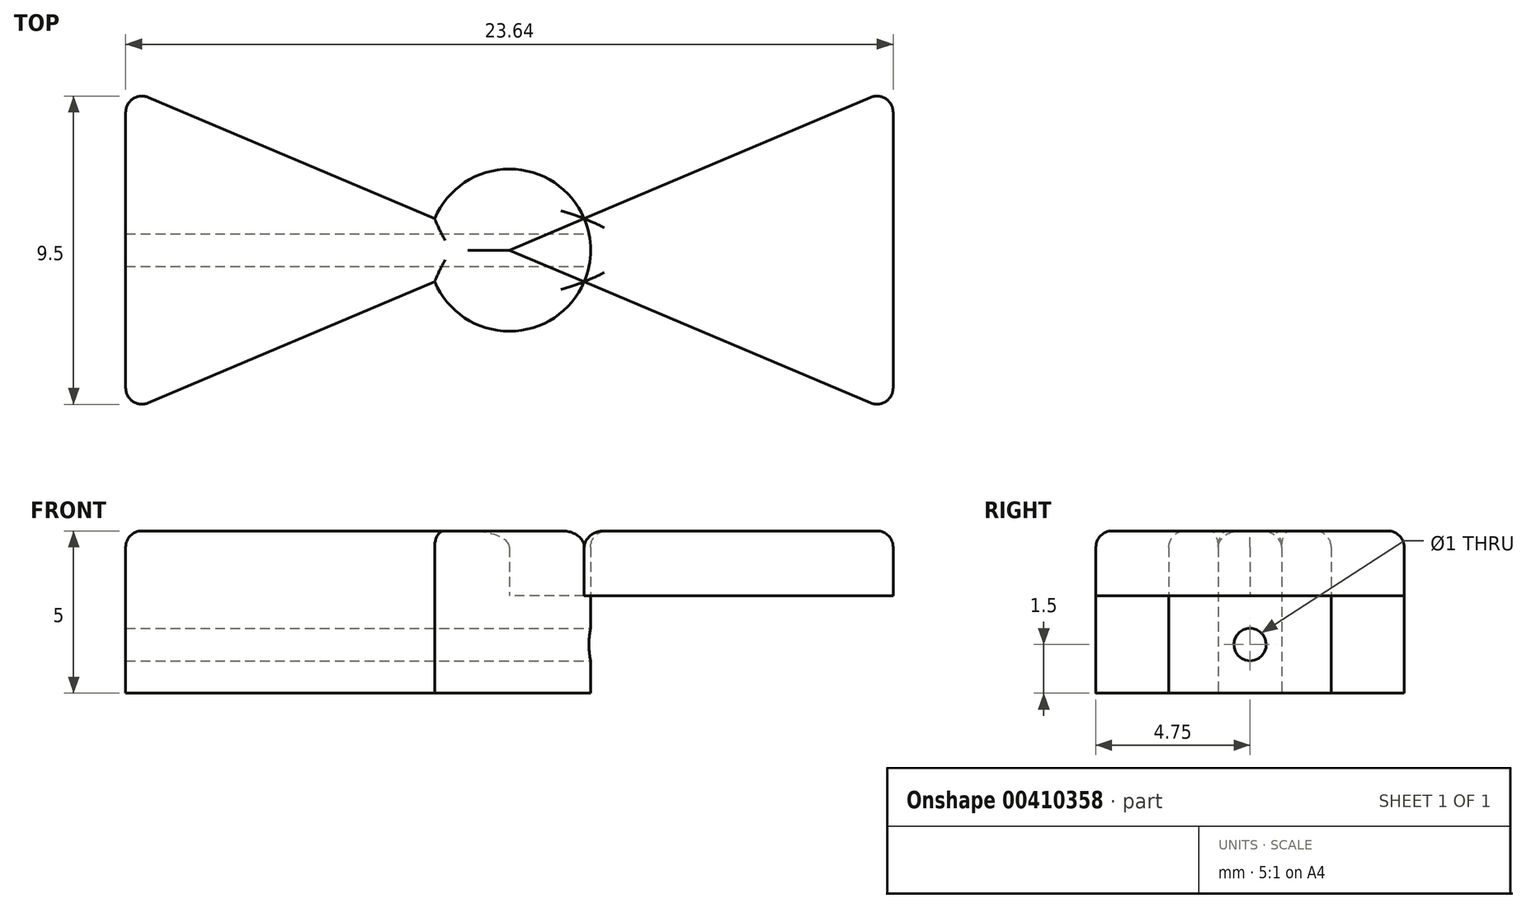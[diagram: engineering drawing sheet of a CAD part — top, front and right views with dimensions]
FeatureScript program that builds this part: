
annotation { "Feature Type Name" : "Feature", "Feature Type Description" : "" }
export const myFeature = defineFeature(function(context is Context, id is Id, definition is map)
    precondition{}
    {
        {
            var Q0;
            Q0=qCreatedBy(makeId("Top.planeOp"),FACE);
            var sketch = newSketch(context, id + "F0", { "sketchPlane" : qUnion([Q0])});
            skCircle(sketch, "E0", {"center": v(0, 0) * mm, "radius": 2.5 * mm});
            skLineSegment(sketch, "E1", {"start": v(-13.8, 0) * mm, "end": v(16.45, 0) * mm, "construction": true});
            skLineSegment(sketch, "E2", {"start": v(0, 11.69) * mm, "end": v(0, -11.19) * mm, "construction": true});
            skLineSegment(sketch, "E3", {"start": v(-11.82, 5) * mm, "end": v(-11.82, -5) * mm});
            skLineSegment(sketch, "E4", {"start": v(-11.82, -5) * mm, "end": v(11.82, 5) * mm});
            skLineSegment(sketch, "E5", {"start": v(11.82, 5) * mm, "end": v(11.82, -5) * mm});
            skLineSegment(sketch, "E6", {"start": v(11.82, -5) * mm, "end": v(-11.82, 5) * mm});
            skLineSegment(sketch, "E7", {"start": v(-11.82, 5) * mm, "end": v(11.82, 5) * mm, "construction": true});
            skSolve(sketch);
        }
        {
            var Q0;
            {var subQ5=sQuery(id+"F0.wireOp",EDGE,"E3");Q0=makeQuery(id+"F0.imprint","IMPRINT",FACE,{"disambiguationData":[TD([[makeQuery(id+"F0.imprint","IMPRINT",EDGE,{"derivedFrom":subQ5}),1.0]])]});}
            var Q1;
            {var subQ3=sQuery(id+"F0.wireOp",EDGE,"E5");Q1=makeQuery(id+"F0.imprint","IMPRINT",FACE,{"disambiguationData":[TD([[makeQuery(id+"F0.imprint","IMPRINT",EDGE,{"derivedFrom":subQ3}),-1.0]])]});}
            var Q2;
            {var subQ0=sQuery(id+"F0.wireOp",EDGE,"E4");var subQ1=sQuery(id+"F0.wireOp",EDGE,"E0");var subQ2=makeQuery(id+"F0.imprint","INTERSECT",VERTEX,{"disambiguationData":[OD(0.0)],"derivedFrom":[subQ1,subQ0]});Q2=makeQuery(id+"F0.imprint","IMPRINT",FACE,{"disambiguationData":[TD([[makeQuery(id+"F0.imprint","IMPRINT",EDGE,{"disambiguationData":[TD([[subQ2,-1.0]])],"derivedFrom":subQ1}),1.0]])]});}
            var Q3;
            {var subQ0=sQuery(id+"F0.wireOp",EDGE,"E4");var subQ1=sQuery(id+"F0.wireOp",EDGE,"E0");var subQ2=makeQuery(id+"F0.imprint","INTERSECT",VERTEX,{"disambiguationData":[OD(1.0)],"derivedFrom":[subQ1,subQ0]});Q3=makeQuery(id+"F0.imprint","IMPRINT",FACE,{"disambiguationData":[TD([[makeQuery(id+"F0.imprint","IMPRINT",EDGE,{"disambiguationData":[TD([[subQ2,-1.0]])],"derivedFrom":subQ1}),1.0]])]});}
            var Q4;
            {var subQ0=sQuery(id+"F0.wireOp",EDGE,"E6");var subQ1=sQuery(id+"F0.wireOp",EDGE,"E0");var subQ2=makeQuery(id+"F0.imprint","INTERSECT",VERTEX,{"disambiguationData":[OD(0.0)],"derivedFrom":[subQ1,subQ0]});Q4=makeQuery(id+"F0.imprint","IMPRINT",FACE,{"disambiguationData":[TD([[makeQuery(id+"F0.imprint","IMPRINT",EDGE,{"disambiguationData":[TD([[subQ2,-1.0]])],"derivedFrom":subQ1}),1.0]])]});}
            var Q5;
            {var subQ1=sQuery(id+"F0.wireOp",EDGE,"E0");var subQ3=makeQuery(id+"F0.imprint","IMPRINT",VERTEX,{"derivedFrom":subQ1});Q5=makeQuery(id+"F0.imprint","IMPRINT",FACE,{"disambiguationData":[TD([[makeQuery(id+"F0.imprint","IMPRINT",EDGE,{"disambiguationData":[TD([[subQ3,-1.0]])],"derivedFrom":subQ1}),1.0]])]});}
            extrude(context, id + "F1", {"entities" : qUnion([Q0, Q1, Q2, Q3, Q4, Q5]), "depth" : 2 * mm, "offsetDistance" : 25 * mm});
        }
        {
            var Q0;
            Q0=makeQuery(id+"F1.opExtrude","CAP_FACE",FACE,{"disambiguationData":[OSD([sQuery(id+"F0.wireOp",EDGE,"E0"),sQuery(id+"F0.wireOp",EDGE,"E3"),sQuery(id+"F0.wireOp",EDGE,"E4"),sQuery(id+"F0.wireOp",EDGE,"E5"),sQuery(id+"F0.wireOp",EDGE,"E6")])],"isStart":true});
            var sketch = newSketch(context, id + "F2", { "sketchPlane" : qUnion([Q0])});
            skCircle(sketch, "E8", {"center": v(0, 0) * mm, "radius": 2.5 * mm});
            skSolve(sketch);
        }
        {
            var Q0;
            Q0 = qSketchRegion(id + "F2", true);
            var Q1;
            {var subQ0=sQuery(id+"F2.wireOp",EDGE,"E8");var subQ1=sQuery(id+"F0.wireOp",EDGE,"E4");var subQ2=sQuery(id+"F0.wireOp",EDGE,"E0");var subQ4=makeQuery(id+"F2.imprint","INTERSECT",VERTEX,{"derivedFrom":[makeQuery(id+"F1.opExtrude","CAP_EDGE",EDGE,{"disambiguationData":[OSD([subQ1]),TDD([makeQuery(id+"F0.imprint","IMPRINT",EDGE,{"disambiguationData":[TD([[makeQuery(id+"F0.imprint","INTERSECT",VERTEX,{"disambiguationData":[OD(0.0)],"derivedFrom":[subQ2,subQ1]}),-1.0]])],"derivedFrom":subQ1})])],"isStart":true}),subQ0]});var subQ5=sQuery(id+"F0.wireOp",EDGE,"E6");var subQ6=sQuery(id+"F0.wireOp",EDGE,"E3");var subQ7=makeQuery(id+"F2.imprint","INTERSECT",VERTEX,{"derivedFrom":[makeQuery(id+"F1.opExtrude","CAP_EDGE",EDGE,{"disambiguationData":[OSD([subQ5]),TDD([makeQuery(id+"F0.imprint","IMPRINT",EDGE,{"disambiguationData":[TD([[makeQuery(id+"F0.imprint","INTERSECT",VERTEX,{"derivedFrom":[subQ6,subQ5]}),1.0]])],"derivedFrom":subQ5})])],"isStart":true}),subQ0]});Q1=makeQuery(id+"F2.imprint","IMPRINT",FACE,{"disambiguationData":[TD([[makeQuery(id+"F2.imprint","IMPRINT",EDGE,{"disambiguationData":[TD([[subQ4,-1.0],[subQ7,1.0]])],"derivedFrom":subQ0}),-1.0]])]});}
            extrude(context, id + "F3", {"entities" : qUnion([Q0, Q1]), "operationType" : NewBodyOperationType.ADD, "depth" : 3 * mm, "offsetDistance" : 25 * mm});
        }
        {
            var Q0;
            Q0=qCreatedBy(makeId("Right.planeOp"),FACE);
            var sketch = newSketch(context, id + "F4", { "sketchPlane" : qUnion([Q0])});
            skCircle(sketch, "E9", {"center": v(0, -1.5) * mm, "radius": 0.5 * mm});
            skSolve(sketch);
        }
        {
            var Q0;
            Q0 = qSketchRegion(id + "F4", true);
            extrude(context, id + "F5", {"entities" : qUnion([Q0]), "operationType" : NewBodyOperationType.REMOVE, "endBound" : BoundingType.SYMMETRIC, "oppositeDirection" : true, "depth" : 25 * mm, "offsetDistance" : 25 * mm});
        }
        {
            var Q0;
            Q0=makeQuery(id+"F1.opExtrude","SWEPT_EDGE",EDGE,{"disambiguationData":[OSD([sQuery(id+"F0.wireOp",EDGE,"E3"),sQuery(id+"F0.wireOp",EDGE,"E4")])]});
            var Q1;
            Q1=makeQuery(id+"F1.opExtrude","SWEPT_EDGE",EDGE,{"disambiguationData":[OSD([sQuery(id+"F0.wireOp",EDGE,"E4"),sQuery(id+"F0.wireOp",EDGE,"E5")])]});
            var Q2;
            Q2=makeQuery(id+"F1.opExtrude","SWEPT_EDGE",EDGE,{"disambiguationData":[OSD([sQuery(id+"F0.wireOp",EDGE,"E5"),sQuery(id+"F0.wireOp",EDGE,"E6")])]});
            var Q3;
            Q3=makeQuery(id+"F1.opExtrude","SWEPT_EDGE",EDGE,{"disambiguationData":[OSD([sQuery(id+"F0.wireOp",EDGE,"E3"),sQuery(id+"F0.wireOp",EDGE,"E6")])]});
            var Q4;
            Q4=makeQuery(id+"F1.opExtrude","CAP_FACE",FACE,{"disambiguationData":[OSD([sQuery(id+"F0.wireOp",EDGE,"E0"),sQuery(id+"F0.wireOp",EDGE,"E3"),sQuery(id+"F0.wireOp",EDGE,"E4"),sQuery(id+"F0.wireOp",EDGE,"E5"),sQuery(id+"F0.wireOp",EDGE,"E6")])],"isStart":false});
            fillet(context, id + "F6", {"entities" : qUnion([Q0, Q1, Q2, Q3, Q4]), "tangentPropagation" : true, "radius" : 0.5 * mm, "defaultsChanged" : false, "vertexSettings" : [], "allowEdgeOverflow" : false});
        }
    });
